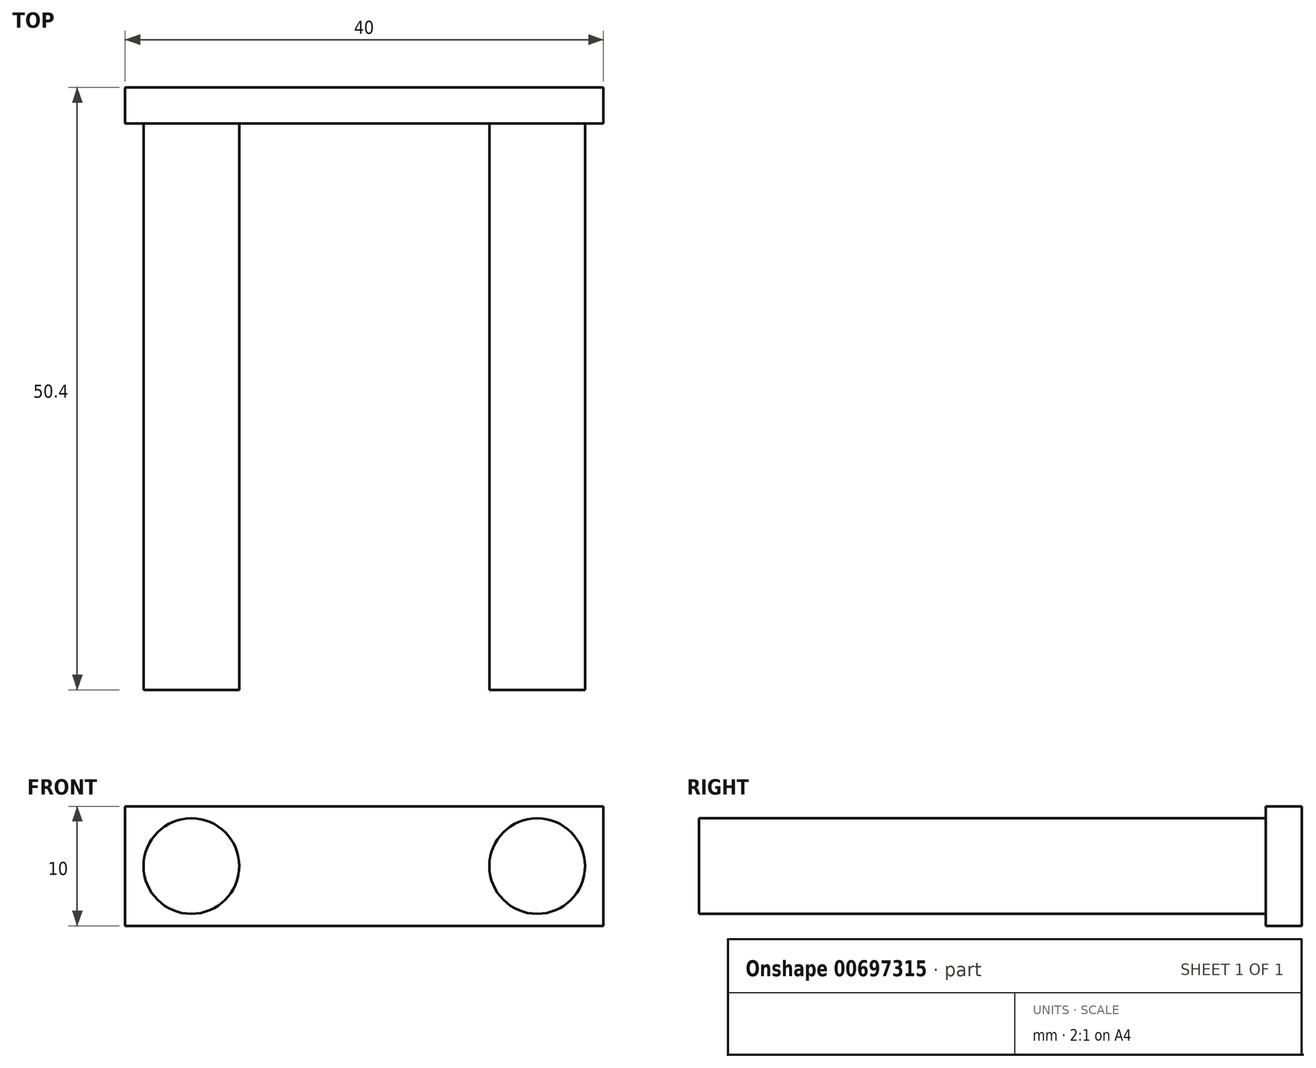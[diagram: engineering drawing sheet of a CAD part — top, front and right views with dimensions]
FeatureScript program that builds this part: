
annotation { "Feature Type Name" : "Feature", "Feature Type Description" : "" }
export const myFeature = defineFeature(function(context is Context, id is Id, definition is map)
    precondition{}
    {
        {
            var Q0;
            Q0=qCreatedBy(makeId("Front.planeOp"),FACE);
            var sketch = newSketch(context, id + "F0", { "sketchPlane" : qUnion([Q0])});
            skLineSegment(sketch, "E0.bottom", {"start": v(20, -5) * mm, "end": v(-20, -5) * mm});
            skLineSegment(sketch, "E0.top", {"start": v(20, 5) * mm, "end": v(-20, 5) * mm});
            skLineSegment(sketch, "E0.left", {"start": v(20, -5) * mm, "end": v(20, 5) * mm});
            skLineSegment(sketch, "E0.right", {"start": v(-20, -5) * mm, "end": v(-20, 5) * mm});
            skPoint(sketch, "E0.middle", {"position": v(0, 0) * mm});
            skSolve(sketch);
        }
        {
            var Q0;
            Q0 = qSketchRegion(id + "F0", true);
            extrude(context, id + "F1", {"entities" : qUnion([Q0]), "depth" : 3 * mm, "offsetDistance" : 25 * mm});
        }
        {
            var Q0;
            Q0=qCreatedBy(makeId("Front.planeOp"),FACE);
            var sketch = newSketch(context, id + "F2", { "sketchPlane" : qUnion([Q0])});
            skCircle(sketch, "E1", {"center": v(-14.46, 0) * mm, "radius": 4 * mm});
            skCircle(sketch, "E2.MirrorC", {"center": v(14.46, 0) * mm, "radius": 4 * mm});
            skSolve(sketch);
        }
        {
            var Q0;
            Q0 = qSketchRegion(id + "F2", true);
            extrude(context, id + "F3", {"entities" : qUnion([Q0]), "operationType" : NewBodyOperationType.ADD, "depth" : 50.4 * mm, "offsetDistance" : 25 * mm});
        }
    });
